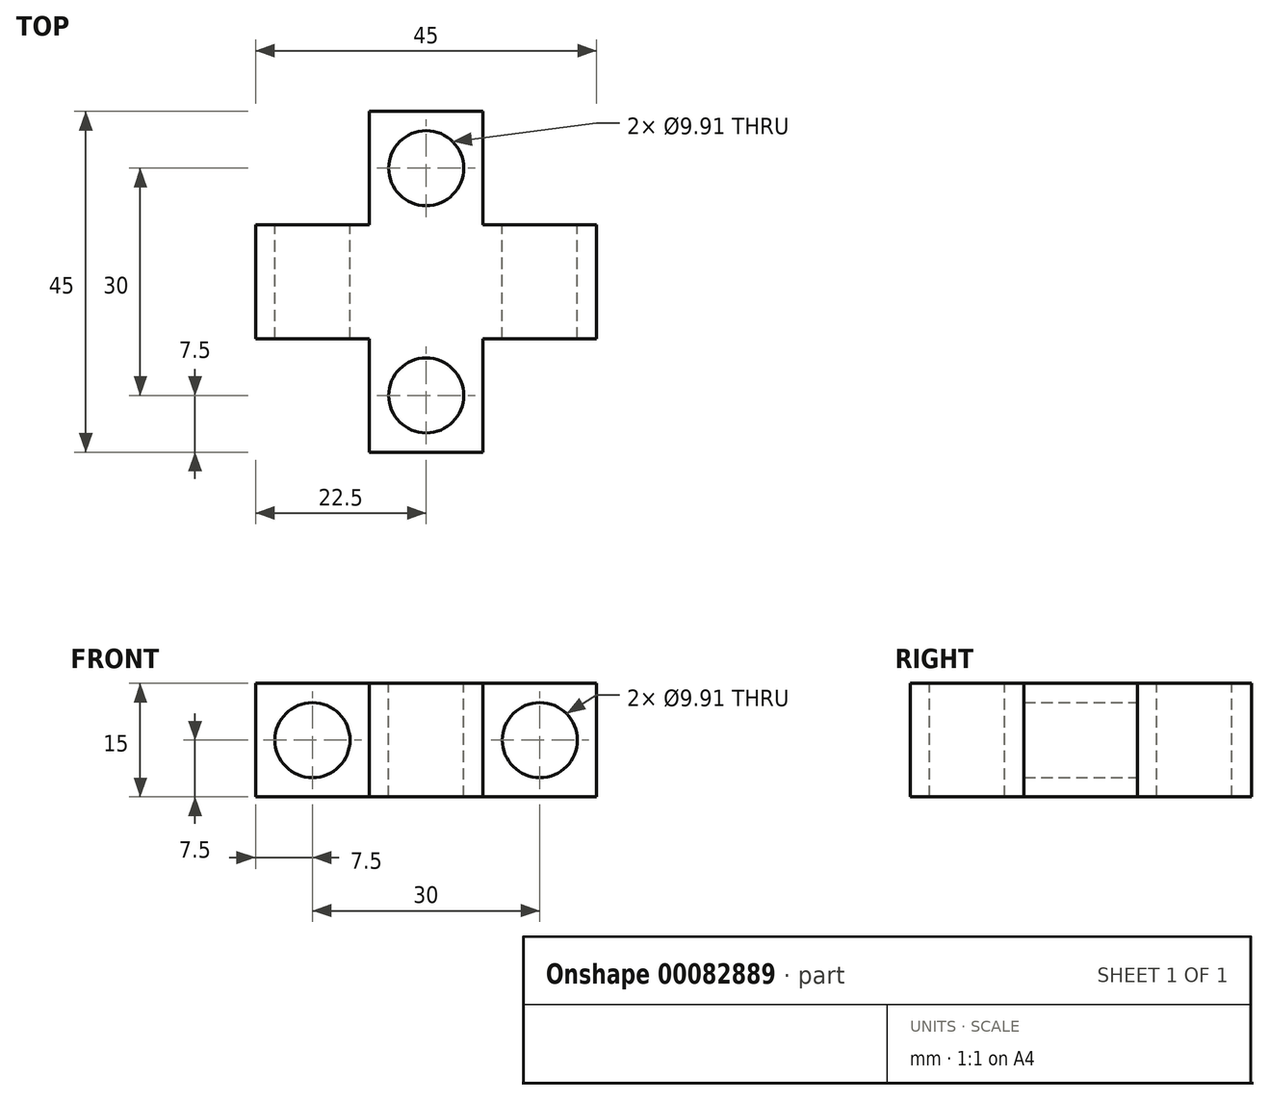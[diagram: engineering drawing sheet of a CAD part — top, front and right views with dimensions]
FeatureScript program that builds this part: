
annotation { "Feature Type Name" : "Feature", "Feature Type Description" : "" }
export const myFeature = defineFeature(function(context is Context, id is Id, definition is map)
    precondition{}
    {
        {
            var Q0;
            Q0=qCreatedBy(makeId("Top.planeOp"),FACE);
            var sketch = newSketch(context, id + "F0", { "sketchPlane" : qUnion([Q0])});
            skLineSegment(sketch, "E0.bottom", {"start": v(22.5, 7.5) * mm, "end": v(-22.5, 7.5) * mm});
            skLineSegment(sketch, "E0.top", {"start": v(22.5, -7.5) * mm, "end": v(-22.5, -7.5) * mm});
            skLineSegment(sketch, "E0.left", {"start": v(22.5, 7.5) * mm, "end": v(22.5, -7.5) * mm});
            skLineSegment(sketch, "E0.right", {"start": v(-22.5, 7.5) * mm, "end": v(-22.5, -7.5) * mm});
            skPoint(sketch, "E0.middle", {"position": v(0, 0) * mm});
            skLineSegment(sketch, "E1.bottom", {"start": v(-7.5, 22.5) * mm, "end": v(7.5, 22.5) * mm});
            skLineSegment(sketch, "E1.top", {"start": v(-7.5, -22.5) * mm, "end": v(7.5, -22.5) * mm});
            skLineSegment(sketch, "E1.left", {"start": v(-7.5, 22.5) * mm, "end": v(-7.5, -22.5) * mm});
            skLineSegment(sketch, "E1.right", {"start": v(7.5, 22.5) * mm, "end": v(7.5, -22.5) * mm});
            skSolve(sketch);
        }
        {
            var Q0;
            {var subQ0=sQuery(id+"F0.wireOp",EDGE,"E0.right");Q0=makeQuery(id+"F0.imprint","IMPRINT",FACE,{"disambiguationData":[TD([[makeQuery(id+"F0.imprint","IMPRINT",EDGE,{"derivedFrom":subQ0}),1.0]])]});}
            var Q1;
            {var subQ0=sQuery(id+"F0.wireOp",EDGE,"E1.right");var subQ1=sQuery(id+"F0.wireOp",EDGE,"E0.bottom");var subQ2=makeQuery(id+"F0.imprint","INTERSECT",VERTEX,{"derivedFrom":[subQ1,subQ0]});Q1=makeQuery(id+"F0.imprint","IMPRINT",FACE,{"disambiguationData":[TD([[makeQuery(id+"F0.imprint","IMPRINT",EDGE,{"disambiguationData":[TD([[subQ2,-1.0]])],"derivedFrom":subQ1}),1.0]])]});}
            var Q2;
            {var subQ0=sQuery(id+"F0.wireOp",EDGE,"E0.left");Q2=makeQuery(id+"F0.imprint","IMPRINT",FACE,{"disambiguationData":[TD([[makeQuery(id+"F0.imprint","IMPRINT",EDGE,{"derivedFrom":subQ0}),-1.0]])]});}
            var Q3;
            {var subQ5=sQuery(id+"F0.wireOp",EDGE,"E1.bottom");Q3=makeQuery(id+"F0.imprint","IMPRINT",FACE,{"disambiguationData":[TD([[makeQuery(id+"F0.imprint","IMPRINT",EDGE,{"derivedFrom":subQ5}),-1.0]])]});}
            var Q4;
            {var subQ5=sQuery(id+"F0.wireOp",EDGE,"E1.top");Q4=makeQuery(id+"F0.imprint","IMPRINT",FACE,{"disambiguationData":[TD([[makeQuery(id+"F0.imprint","IMPRINT",EDGE,{"derivedFrom":subQ5}),1.0]])]});}
            extrude(context, id + "F1", {"entities" : qUnion([Q0, Q1, Q2, Q3, Q4]), "depth" : 15 * mm});
        }
        {
            var Q0;
            Q0=makeQuery(id+"F1.opExtrude","CAP_FACE",FACE,{"disambiguationData":[OSD([sQuery(id+"F0.wireOp",EDGE,"E0.bottom"),sQuery(id+"F0.wireOp",EDGE,"E0.top"),sQuery(id+"F0.wireOp",EDGE,"E0.left"),sQuery(id+"F0.wireOp",EDGE,"E0.right"),sQuery(id+"F0.wireOp",EDGE,"E1.bottom"),sQuery(id+"F0.wireOp",EDGE,"E1.top"),sQuery(id+"F0.wireOp",EDGE,"E1.left"),sQuery(id+"F0.wireOp",EDGE,"E1.right")])],"isStart":false});
            var sketch = newSketch(context, id + "F2", { "sketchPlane" : qUnion([Q0])});
            skCircle(sketch, "E2", {"center": v(0, -15) * mm, "radius": 4.96 * mm});
            skCircle(sketch, "E3", {"center": v(0, 15) * mm, "radius": 4.96 * mm});
            skPoint(sketch, "E4", {"position": v(-22.5, 0) * mm});
            skLineSegment(sketch, "E5", {"start": v(7.5, -15) * mm, "end": v(-7.5, -15) * mm, "construction": true});
            skLineSegment(sketch, "E6", {"start": v(7.5, 15) * mm, "end": v(-7.5, 15) * mm, "construction": true});
            skSolve(sketch);
        }
        {
            var Q0;
            Q0=qSketchRegion(id+"F2",true);
            extrude(context, id + "F3", {"entities" : qUnion([Q0]), "operationType" : NewBodyOperationType.REMOVE, "endBound" : BoundingType.THROUGH_ALL, "oppositeDirection" : true, "depth" : 25 * mm});
        }
        {
            var Q0;
            {var subQ0=sQuery(id+"F0.wireOp",EDGE,"E0.bottom");Q0=makeQuery(id+"F1.opExtrude","SWEPT_FACE",FACE,{"disambiguationData":[OSD([subQ0]),TDD([makeQuery(id+"F0.imprint","IMPRINT",EDGE,{"disambiguationData":[TD([[makeQuery(id+"F0.imprint","INTERSECT",VERTEX,{"derivedFrom":[subQ0,sQuery(id+"F0.wireOp",EDGE,"E0.right")]}),1.0]])],"derivedFrom":subQ0})])]});}
            var sketch = newSketch(context, id + "F4", { "sketchPlane" : qUnion([Q0])});
            skLineSegment(sketch, "E7", {"start": v(15, 0) * mm, "end": v(15, 15) * mm, "construction": true});
            skLineSegment(sketch, "E8", {"start": v(0, 24.89) * mm, "end": v(0, 0) * mm, "construction": true});
            skLineSegment(sketch, "E9", {"start": v(-15, 0) * mm, "end": v(-15, 15) * mm, "construction": true});
            skCircle(sketch, "E10", {"center": v(15, 7.5) * mm, "radius": 4.96 * mm});
            skCircle(sketch, "E11", {"center": v(-15, 7.5) * mm, "radius": 4.96 * mm});
            skSolve(sketch);
        }
        {
            var Q0;
            Q0 = qSketchRegion(id + "F4", true);
            extrude(context, id + "F5", {"entities" : qUnion([Q0]), "operationType" : NewBodyOperationType.REMOVE, "endBound" : BoundingType.THROUGH_ALL, "oppositeDirection" : true, "depth" : 25 * mm});
        }
    });
